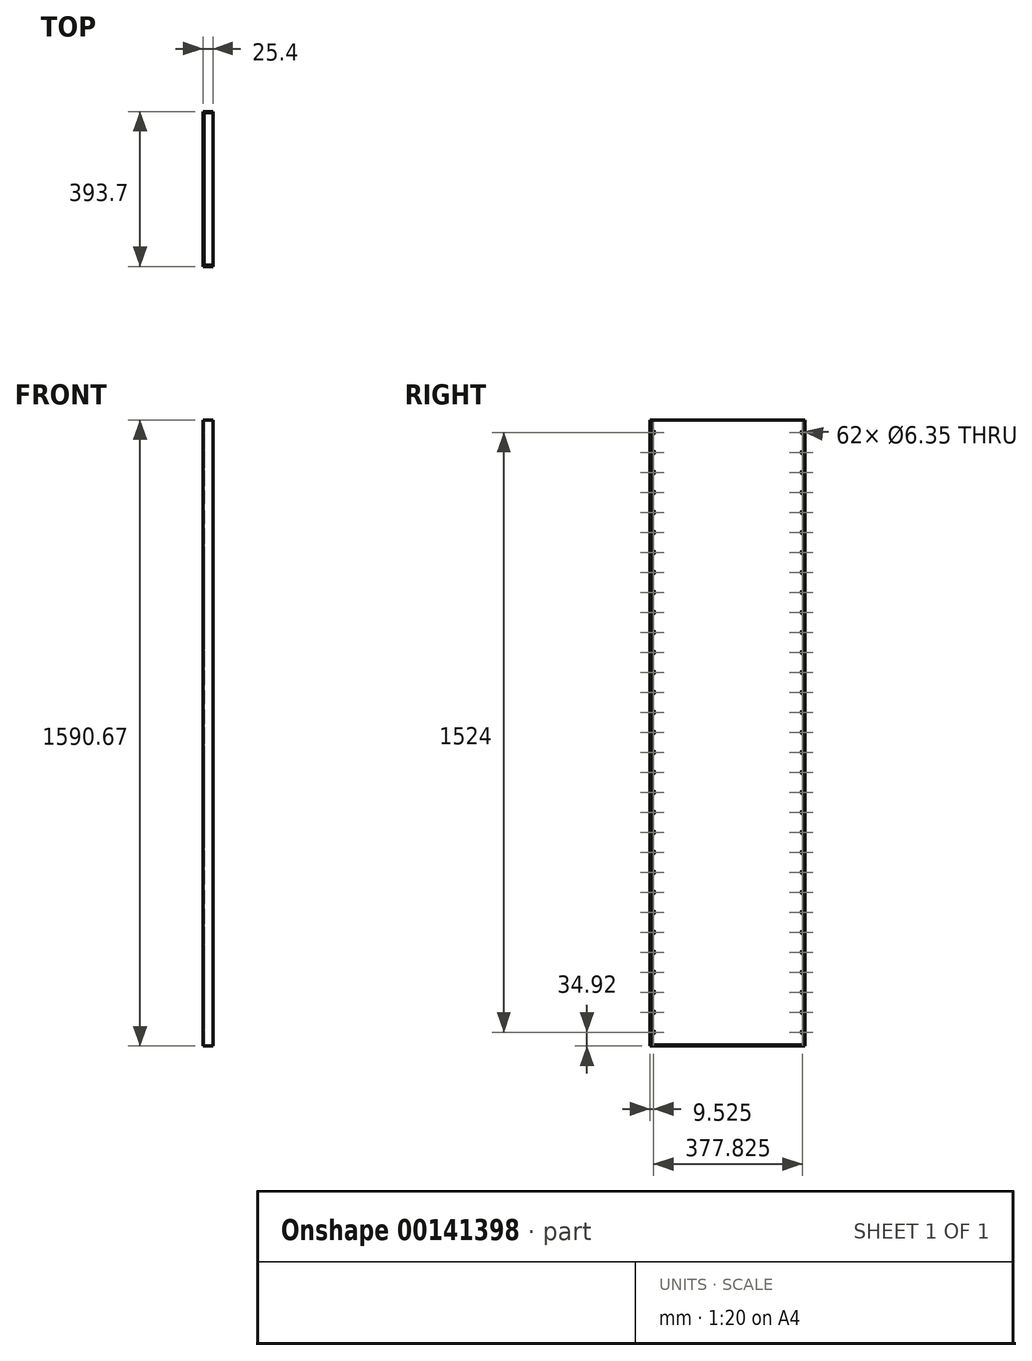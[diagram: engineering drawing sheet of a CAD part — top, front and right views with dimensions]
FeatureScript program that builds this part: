
annotation { "Feature Type Name" : "Feature", "Feature Type Description" : "" }
export const myFeature = defineFeature(function(context is Context, id is Id, definition is map)
    precondition{}
    {
        {
            var Q0;
            Q0=qCreatedBy(makeId("Top.planeOp"),FACE);
            var sketch = newSketch(context, id + "F0", { "sketchPlane" : qUnion([Q0])});
            skLineSegment(sketch, "E0", {"start": v(0, 196.85) * mm, "end": v(0, -196.85) * mm});
            skLineSegment(sketch, "E1", {"start": v(0, 196.85) * mm, "end": v(25.4, 196.85) * mm});
            skLineSegment(sketch, "E2", {"start": v(25.4, 196.85) * mm, "end": v(25.4, 193.68) * mm});
            skLineSegment(sketch, "E3", {"start": v(25.4, 193.68) * mm, "end": v(3.17, 193.68) * mm});
            skLineSegment(sketch, "E4", {"start": v(3.18, 193.68) * mm, "end": v(3.18, -193.68) * mm});
            skLineSegment(sketch, "E5", {"start": v(3.18, -193.68) * mm, "end": v(25.4, -193.68) * mm});
            skLineSegment(sketch, "E6", {"start": v(25.4, -193.68) * mm, "end": v(25.4, -196.85) * mm});
            skLineSegment(sketch, "E7", {"start": v(25.4, -196.85) * mm, "end": v(0, -196.85) * mm});
            skSolve(sketch);
        }
        {
            var Q0;
            Q0 = qSketchRegion(id + "F0", true);
            extrude(context, id + "F1", {"entities" : qUnion([Q0]), "depth" : 1587.5 * mm});
        }
        {
            var Q0;
            Q0=makeQuery(id+"F1.opExtrude","SWEPT_FACE",FACE,{"disambiguationData":[OSD([sQuery(id+"F0.wireOp",EDGE,"E0")])]});
            var sketch = newSketch(context, id + "F2", { "sketchPlane" : qUnion([Q0])});
            skCircle(sketch, "E8", {"center": v(187.33, 793.75) * mm, "radius": 3.18 * mm});
            skLineSegment(sketch, "E9", {"start": v(196.85, 793.75) * mm, "end": v(-196.85, 793.75) * mm});
            skCircle(sketch, "E10.0.1.0", {"center": v(187.33, 844.55) * mm, "radius": 3.18 * mm});
            skCircle(sketch, "E10.0.2.0", {"center": v(187.33, 895.35) * mm, "radius": 3.18 * mm});
            skCircle(sketch, "E10.0.3.0", {"center": v(187.33, 946.15) * mm, "radius": 3.18 * mm});
            skCircle(sketch, "E10.0.4.0", {"center": v(187.33, 996.95) * mm, "radius": 3.18 * mm});
            skCircle(sketch, "E10.0.5.0", {"center": v(187.33, 1047.75) * mm, "radius": 3.18 * mm});
            skCircle(sketch, "E10.0.6.0", {"center": v(187.33, 1098.55) * mm, "radius": 3.18 * mm});
            skCircle(sketch, "E10.0.7.0", {"center": v(187.33, 1149.35) * mm, "radius": 3.18 * mm});
            skCircle(sketch, "E10.0.8.0", {"center": v(187.33, 1200.15) * mm, "radius": 3.18 * mm});
            skCircle(sketch, "E10.0.9.0", {"center": v(187.33, 1250.95) * mm, "radius": 3.18 * mm});
            skCircle(sketch, "E10.0.10.0", {"center": v(187.33, 1301.75) * mm, "radius": 3.18 * mm});
            skCircle(sketch, "E10.0.11.0", {"center": v(187.33, 1352.55) * mm, "radius": 3.18 * mm});
            skCircle(sketch, "E10.0.12.0", {"center": v(187.33, 1403.35) * mm, "radius": 3.18 * mm});
            skCircle(sketch, "E10.0.13.0", {"center": v(187.33, 1454.15) * mm, "radius": 3.18 * mm});
            skCircle(sketch, "E10.0.14.0", {"center": v(187.33, 1504.95) * mm, "radius": 3.18 * mm});
            skCircle(sketch, "E10.1.0.0", {"center": v(-190.5, 793.75) * mm, "radius": 3.18 * mm});
            skCircle(sketch, "E10.1.1.0", {"center": v(-190.5, 844.55) * mm, "radius": 3.18 * mm});
            skCircle(sketch, "E10.1.2.0", {"center": v(-190.5, 895.35) * mm, "radius": 3.18 * mm});
            skCircle(sketch, "E10.1.3.0", {"center": v(-190.5, 946.15) * mm, "radius": 3.18 * mm});
            skCircle(sketch, "E10.1.4.0", {"center": v(-190.5, 996.95) * mm, "radius": 3.18 * mm});
            skCircle(sketch, "E10.1.5.0", {"center": v(-190.5, 1047.75) * mm, "radius": 3.18 * mm});
            skCircle(sketch, "E10.1.6.0", {"center": v(-190.5, 1098.55) * mm, "radius": 3.18 * mm});
            skCircle(sketch, "E10.1.7.0", {"center": v(-190.5, 1149.35) * mm, "radius": 3.18 * mm});
            skCircle(sketch, "E10.1.8.0", {"center": v(-190.5, 1200.15) * mm, "radius": 3.18 * mm});
            skCircle(sketch, "E10.1.9.0", {"center": v(-190.5, 1250.95) * mm, "radius": 3.18 * mm});
            skCircle(sketch, "E10.1.10.0", {"center": v(-190.5, 1301.75) * mm, "radius": 3.18 * mm});
            skCircle(sketch, "E10.1.11.0", {"center": v(-190.5, 1352.55) * mm, "radius": 3.18 * mm});
            skCircle(sketch, "E10.1.12.0", {"center": v(-190.5, 1403.35) * mm, "radius": 3.18 * mm});
            skCircle(sketch, "E10.1.13.0", {"center": v(-190.5, 1454.15) * mm, "radius": 3.18 * mm});
            skCircle(sketch, "E10.1.14.0", {"center": v(-190.5, 1504.95) * mm, "radius": 3.18 * mm});
            skLineSegment(sketch, "E10.direction1", {"start": v(187.33, 793.75) * mm, "end": v(-190.5, 793.75) * mm, "construction": true});
            skLineSegment(sketch, "E10.direction2", {"start": v(187.33, 793.75) * mm, "end": v(187.33, 844.55) * mm, "construction": true});
            skCircle(sketch, "E11.0.1.0", {"center": v(187.33, 742.95) * mm, "radius": 3.18 * mm});
            skCircle(sketch, "E11.0.2.0", {"center": v(187.33, 692.15) * mm, "radius": 3.18 * mm});
            skCircle(sketch, "E11.0.3.0", {"center": v(187.33, 641.35) * mm, "radius": 3.18 * mm});
            skCircle(sketch, "E11.0.4.0", {"center": v(187.33, 590.55) * mm, "radius": 3.18 * mm});
            skCircle(sketch, "E11.0.5.0", {"center": v(187.33, 539.75) * mm, "radius": 3.18 * mm});
            skCircle(sketch, "E11.0.6.0", {"center": v(187.33, 488.95) * mm, "radius": 3.18 * mm});
            skCircle(sketch, "E11.0.7.0", {"center": v(187.33, 438.15) * mm, "radius": 3.18 * mm});
            skCircle(sketch, "E11.0.8.0", {"center": v(187.33, 387.35) * mm, "radius": 3.18 * mm});
            skCircle(sketch, "E11.0.9.0", {"center": v(187.33, 336.55) * mm, "radius": 3.18 * mm});
            skCircle(sketch, "E11.0.10.0", {"center": v(187.33, 285.75) * mm, "radius": 3.18 * mm});
            skCircle(sketch, "E11.0.11.0", {"center": v(187.33, 234.95) * mm, "radius": 3.18 * mm});
            skCircle(sketch, "E11.0.12.0", {"center": v(187.33, 184.15) * mm, "radius": 3.18 * mm});
            skCircle(sketch, "E11.0.13.0", {"center": v(187.33, 133.35) * mm, "radius": 3.18 * mm});
            skCircle(sketch, "E11.0.14.0", {"center": v(187.33, 82.55) * mm, "radius": 3.18 * mm});
            skCircle(sketch, "E11.1.1.0", {"center": v(-190.5, 742.95) * mm, "radius": 3.18 * mm});
            skCircle(sketch, "E11.1.2.0", {"center": v(-190.5, 692.15) * mm, "radius": 3.18 * mm});
            skCircle(sketch, "E11.1.3.0", {"center": v(-190.5, 641.35) * mm, "radius": 3.18 * mm});
            skCircle(sketch, "E11.1.4.0", {"center": v(-190.5, 590.55) * mm, "radius": 3.18 * mm});
            skCircle(sketch, "E11.1.5.0", {"center": v(-190.5, 539.75) * mm, "radius": 3.18 * mm});
            skCircle(sketch, "E11.1.6.0", {"center": v(-190.5, 488.95) * mm, "radius": 3.18 * mm});
            skCircle(sketch, "E11.1.7.0", {"center": v(-190.5, 438.15) * mm, "radius": 3.18 * mm});
            skCircle(sketch, "E11.1.8.0", {"center": v(-190.5, 387.35) * mm, "radius": 3.18 * mm});
            skCircle(sketch, "E11.1.9.0", {"center": v(-190.5, 336.55) * mm, "radius": 3.18 * mm});
            skCircle(sketch, "E11.1.10.0", {"center": v(-190.5, 285.75) * mm, "radius": 3.18 * mm});
            skCircle(sketch, "E11.1.11.0", {"center": v(-190.5, 234.95) * mm, "radius": 3.18 * mm});
            skCircle(sketch, "E11.1.12.0", {"center": v(-190.5, 184.15) * mm, "radius": 3.18 * mm});
            skCircle(sketch, "E11.1.13.0", {"center": v(-190.5, 133.35) * mm, "radius": 3.18 * mm});
            skCircle(sketch, "E11.1.14.0", {"center": v(-190.5, 82.55) * mm, "radius": 3.18 * mm});
            skLineSegment(sketch, "E11.direction2", {"start": v(187.33, 793.75) * mm, "end": v(187.33, 742.95) * mm, "construction": true});
            skCircle(sketch, "E12.0.0.15", {"center": v(187.33, 31.75) * mm, "radius": 3.18 * mm});
            skCircle(sketch, "E12.0.1.15", {"center": v(-190.5, 31.75) * mm, "radius": 3.18 * mm});
            skCircle(sketch, "E13.0.0.15", {"center": v(187.33, 1555.75) * mm, "radius": 3.18 * mm});
            skCircle(sketch, "E13.0.1.15", {"center": v(-190.5, 1555.75) * mm, "radius": 3.18 * mm});
            skSolve(sketch);
        }
        {
            var Q0;
            Q0 = qSketchRegion(id + "F2", true);
            extrude(context, id + "F3", {"entities" : qUnion([Q0]), "operationType" : NewBodyOperationType.REMOVE, "endBound" : BoundingType.THROUGH_ALL, "oppositeDirection" : true, "depth" : 25.4 * mm});
        }
        {
            var Q0;
            Q0=makeQuery(id+"F1.opExtrude","CAP_FACE",FACE,{"disambiguationData":[OSD([sQuery(id+"F0.wireOp",EDGE,"E0"),sQuery(id+"F0.wireOp",EDGE,"E1"),sQuery(id+"F0.wireOp",EDGE,"E2"),sQuery(id+"F0.wireOp",EDGE,"E3"),sQuery(id+"F0.wireOp",EDGE,"E4"),sQuery(id+"F0.wireOp",EDGE,"E5"),sQuery(id+"F0.wireOp",EDGE,"E6"),sQuery(id+"F0.wireOp",EDGE,"E7")])],"isStart":true});
            var sketch = newSketch(context, id + "F4", { "sketchPlane" : qUnion([Q0])});
            skLineSegment(sketch, "E14.bottom", {"start": v(0, 196.85) * mm, "end": v(25.4, 196.85) * mm});
            skLineSegment(sketch, "E14.top", {"start": v(0, -196.85) * mm, "end": v(25.4, -196.85) * mm});
            skLineSegment(sketch, "E14.left", {"start": v(0, 196.85) * mm, "end": v(0, -196.85) * mm});
            skLineSegment(sketch, "E14.right", {"start": v(25.4, 196.85) * mm, "end": v(25.4, -196.85) * mm});
            skSolve(sketch);
        }
        {
            var Q0;
            Q0 = qSketchRegion(id + "F4", true);
            extrude(context, id + "F5", {"entities" : qUnion([Q0]), "operationType" : NewBodyOperationType.ADD, "depth" : 3.17 * mm});
        }
    });
